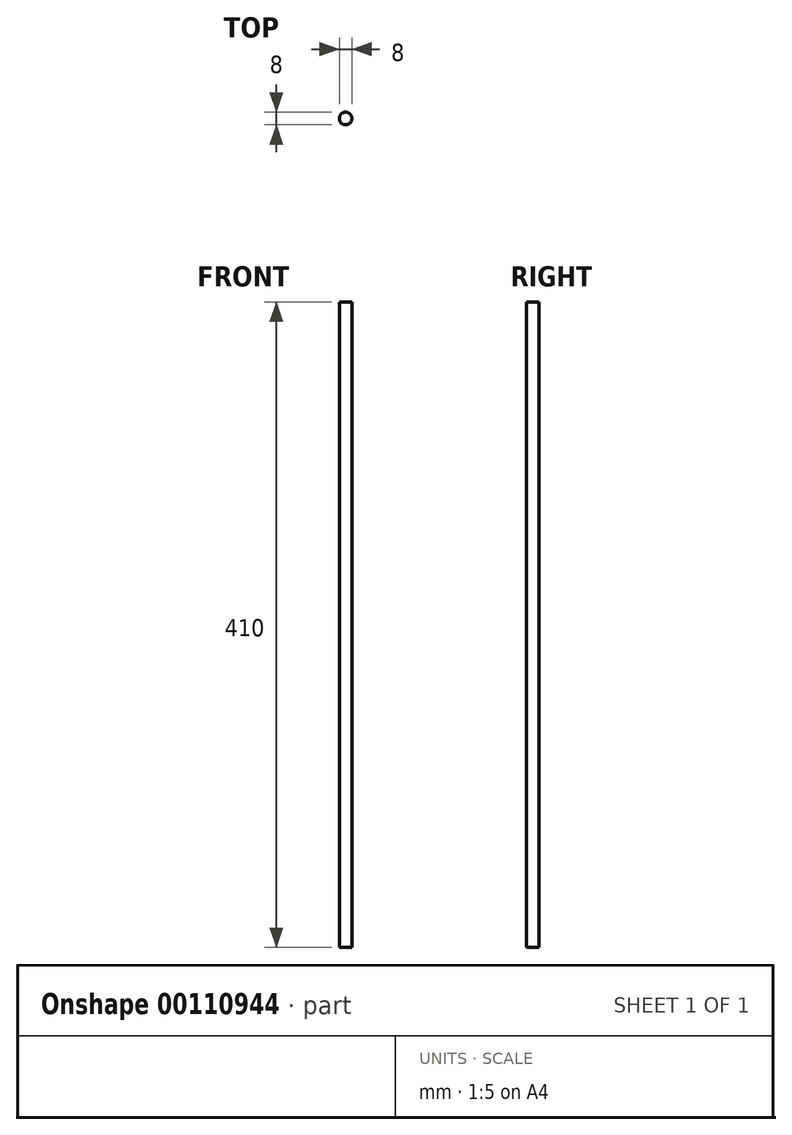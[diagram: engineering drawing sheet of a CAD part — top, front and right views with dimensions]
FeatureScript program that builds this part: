
annotation { "Feature Type Name" : "Feature", "Feature Type Description" : "" }
export const myFeature = defineFeature(function(context is Context, id is Id, definition is map)
    precondition{}
    {
        {
            var Q0;
            Q0=qCreatedBy(makeId("Top.planeOp"),FACE);
            var sketch = newSketch(context, id + "F0", { "sketchPlane" : qUnion([Q0])});
            skCircle(sketch, "E0", {"center": v(0, 0) * mm, "radius": 4 * mm});
            skSolve(sketch);
        }
        {
            var Q0;
            Q0=qSketchRegion(id+"F0",true);
            extrude(context, id + "F1", {"entities" : qUnion([Q0]), "depth" : 410 * mm});
        }
    });
